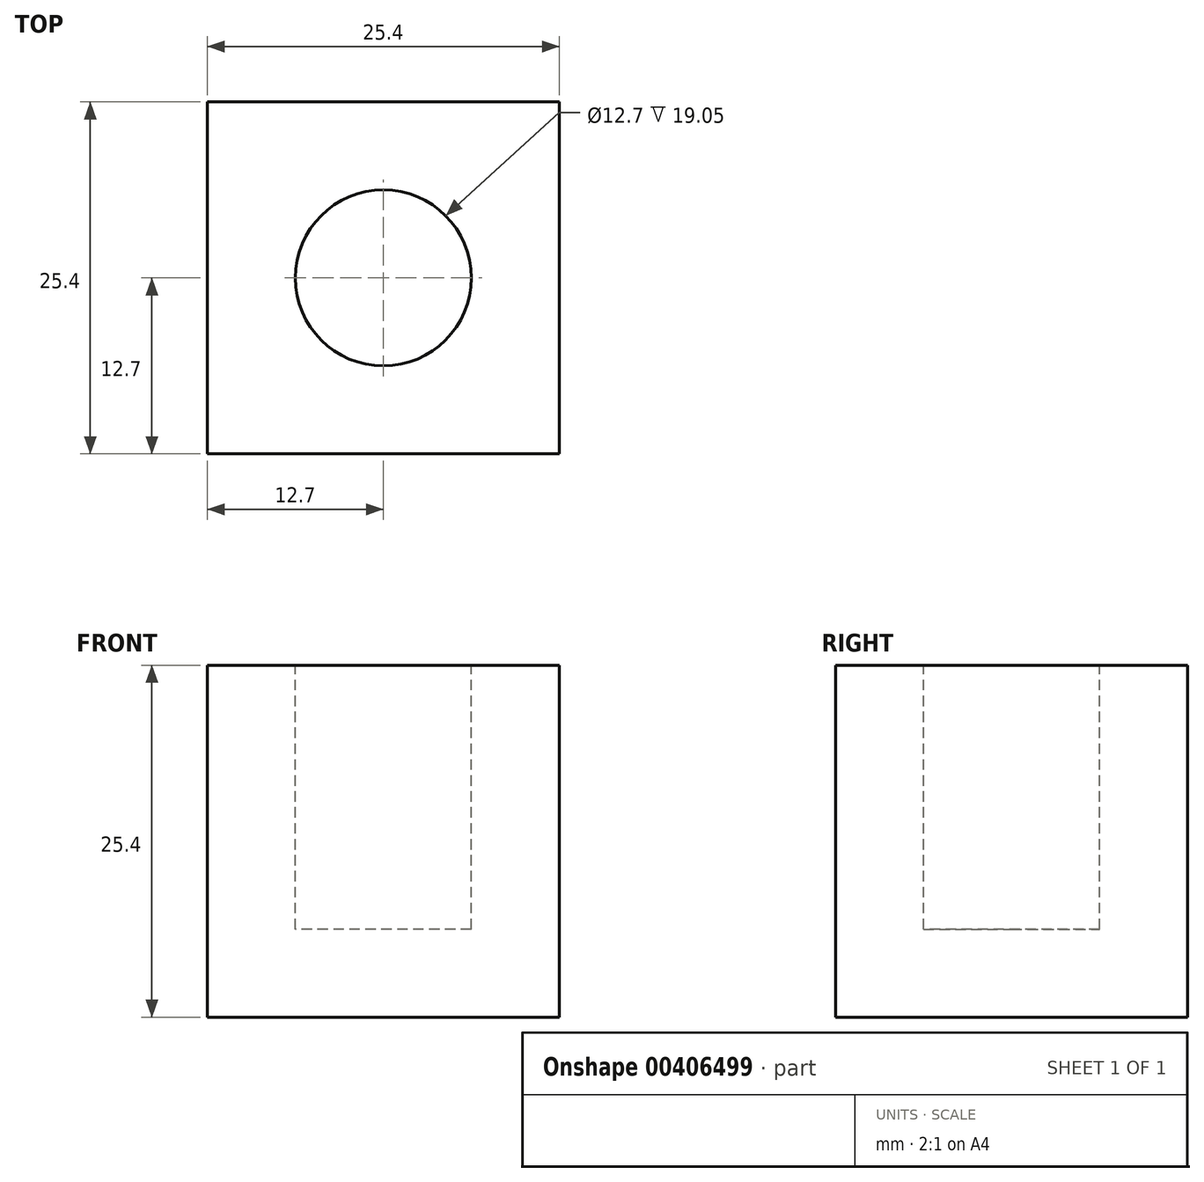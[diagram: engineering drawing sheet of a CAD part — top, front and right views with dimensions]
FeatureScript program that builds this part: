
annotation { "Feature Type Name" : "Feature", "Feature Type Description" : "" }
export const myFeature = defineFeature(function(context is Context, id is Id, definition is map)
    precondition{}
    {
        {
            var Q0;
            Q0=qCreatedBy(makeId("Front.planeOp"),FACE);
            var sketch = newSketch(context, id + "F0", { "sketchPlane" : qUnion([Q0])});
            skLineSegment(sketch, "E0.bottom", {"start": v(12.7, -12.7) * mm, "end": v(-12.7, -12.7) * mm});
            skLineSegment(sketch, "E0.top", {"start": v(12.7, 12.7) * mm, "end": v(-12.7, 12.7) * mm});
            skLineSegment(sketch, "E0.left", {"start": v(12.7, -12.7) * mm, "end": v(12.7, 12.7) * mm});
            skLineSegment(sketch, "E0.right", {"start": v(-12.7, -12.7) * mm, "end": v(-12.7, 12.7) * mm});
            skPoint(sketch, "E0.middle", {"position": v(0, 0) * mm});
            skSolve(sketch);
        }
        {
            var Q0;
            Q0=makeQuery(id+"F0.imprint","IMPRINT",FACE,{"disambiguationData":[TD([[makeQuery(id+"F0.imprint","IMPRINT",EDGE,{"derivedFrom":sQuery(id+"F0.wireOp",EDGE,"E0.bottom")}),-1.0]])]});
            extrude(context, id + "F1", {"entities" : qUnion([Q0]), "depth" : 25.4 * mm});
        }
        {
            var Q0;
            Q0=makeQuery(id+"F1.opExtrude","SWEPT_FACE",FACE,{"disambiguationData":[OSD([sQuery(id+"F0.wireOp",EDGE,"E0.top")])]});
            var sketch = newSketch(context, id + "F2", { "sketchPlane" : qUnion([Q0])});
            skCircle(sketch, "E1", {"center": v(0, -12.7) * mm, "radius": 6.35 * mm});
            skPoint(sketch, "E1.centerSnap0", {"position": v(12.7, -12.7) * mm});
            skSolve(sketch);
        }
        {
            var Q0;
            Q0=makeQuery(id+"F2.imprint","IMPRINT",FACE,{"disambiguationData":[TD([[makeQuery(id+"F2.imprint","IMPRINT",EDGE,{"derivedFrom":sQuery(id+"F2.wireOp",EDGE,"E1")}),1.0]])]});
            extrude(context, id + "F3", {"entities" : qUnion([Q0]), "operationType" : NewBodyOperationType.REMOVE, "oppositeDirection" : true, "depth" : 19.05 * mm});
        }
    });
